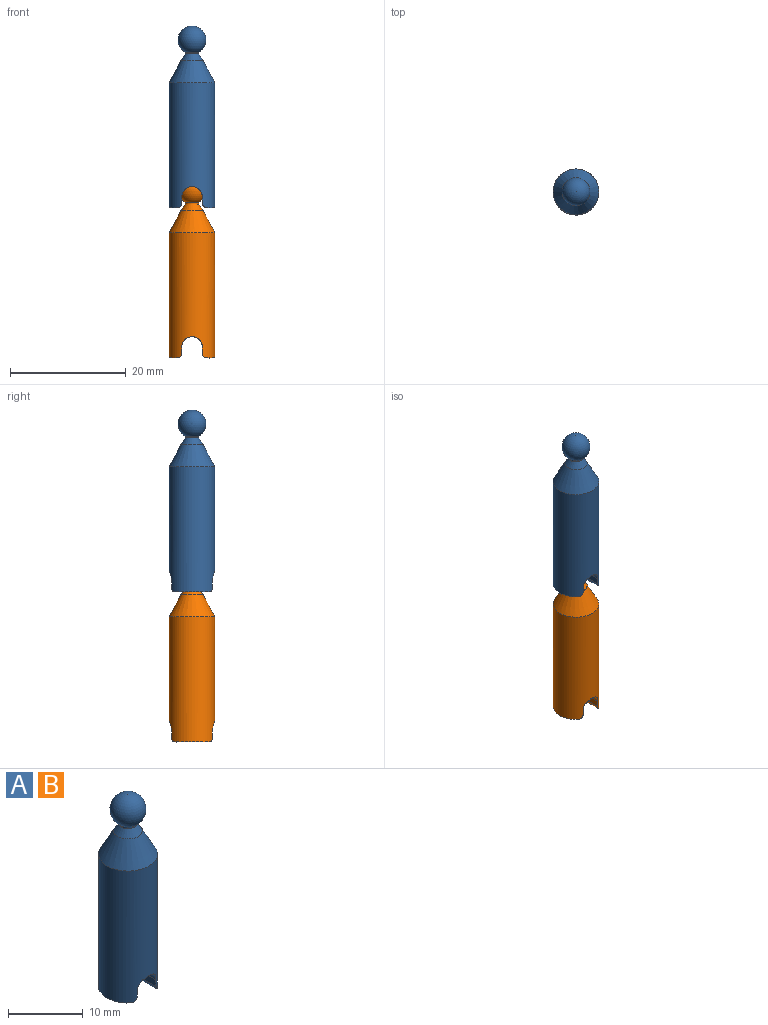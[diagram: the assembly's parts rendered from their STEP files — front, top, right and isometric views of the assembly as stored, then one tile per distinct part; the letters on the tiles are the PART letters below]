
ASSEMBLY  parts=2 mates=1
PART A: 16 faces, bbox 7.9x7.9x31.4 mm
  f0: plane 5.91x1.33mm, normal (0,0,-1), area 5.5mm2, adj f4,f15
  f1: plane 5.91x1.33mm, normal (0,0,-1), area 5.5mm2, adj f4,f14
  f2: plane 7.03x1.08mm, normal (1,0,0), area 4.8mm2, adj f4,f5,f10,f11,f12,f14
  f3: plane 7.03x1.08mm, normal (-1,0,0), area 4.8mm2, adj f4,f5,f10,f11,f13,f15
  f4: cylinder r=3.94mm len=21.59mm, axis (0,0,-1), area 509.1mm2, adj f0,f1,f2,f3,f6,f10,f11,f14
  f5: torus R=0mm, axis (0,0,-1), area 73.6mm2, adj f2,f3,f10,f11,f12,f13
  f6: cone r=1.91mm half-angle=28.1deg, axis (0,0,-1), area 79.2mm2, adj f4,f7
  f7: cone r=1.91mm half-angle=33.7deg, axis (0,0,-1), area 13.2mm2, adj f6,f8
  f8: cylinder r=1.14mm len=2.29mm, axis (0,0,-1), area 2.1mm2, adj f7,f9
  f9: sphere r=2.41mm, area 68.8mm2, adj f8
  f10: cylinder r=1.78mm len=3.56mm, axis (0,-1,0), area 6.5mm2, adj f2,f3,f4,f5
  f11: cylinder r=1.78mm len=3.56mm, axis (0,-1,0), area 6.5mm2, adj f2,f3,f4,f5
  f12: plane 1.32x0.12mm, normal (0,0,1), area 0.1mm2, adj f2,f5
  f13: plane 1.32x0.12mm, normal (0,0,1), area 0.1mm2, adj f3,f5
  f14: cylinder r=0.83mm len=7.03mm, axis (0,-1,0), area 8.6mm2, adj f1,f2,f4
  f15: cylinder r=0.83mm len=7.03mm, axis (0,1,0), area 8.6mm2, adj f0,f3,f4
PART B: same geometry as A
PLACE A rot(axis=(-0.7,0.72,-0.06),0deg) t=(-5.93,-22.11,-48.23)mm
PLACE B rot(axis=(-0.7,0.72,-0.06),0deg) t=(-5.93,-22.11,-74.11)mm
MATE revolute A.f5 <-> B.f6  axis (0,0,-1) through (-5.93,-22.11,-47.28)mm
